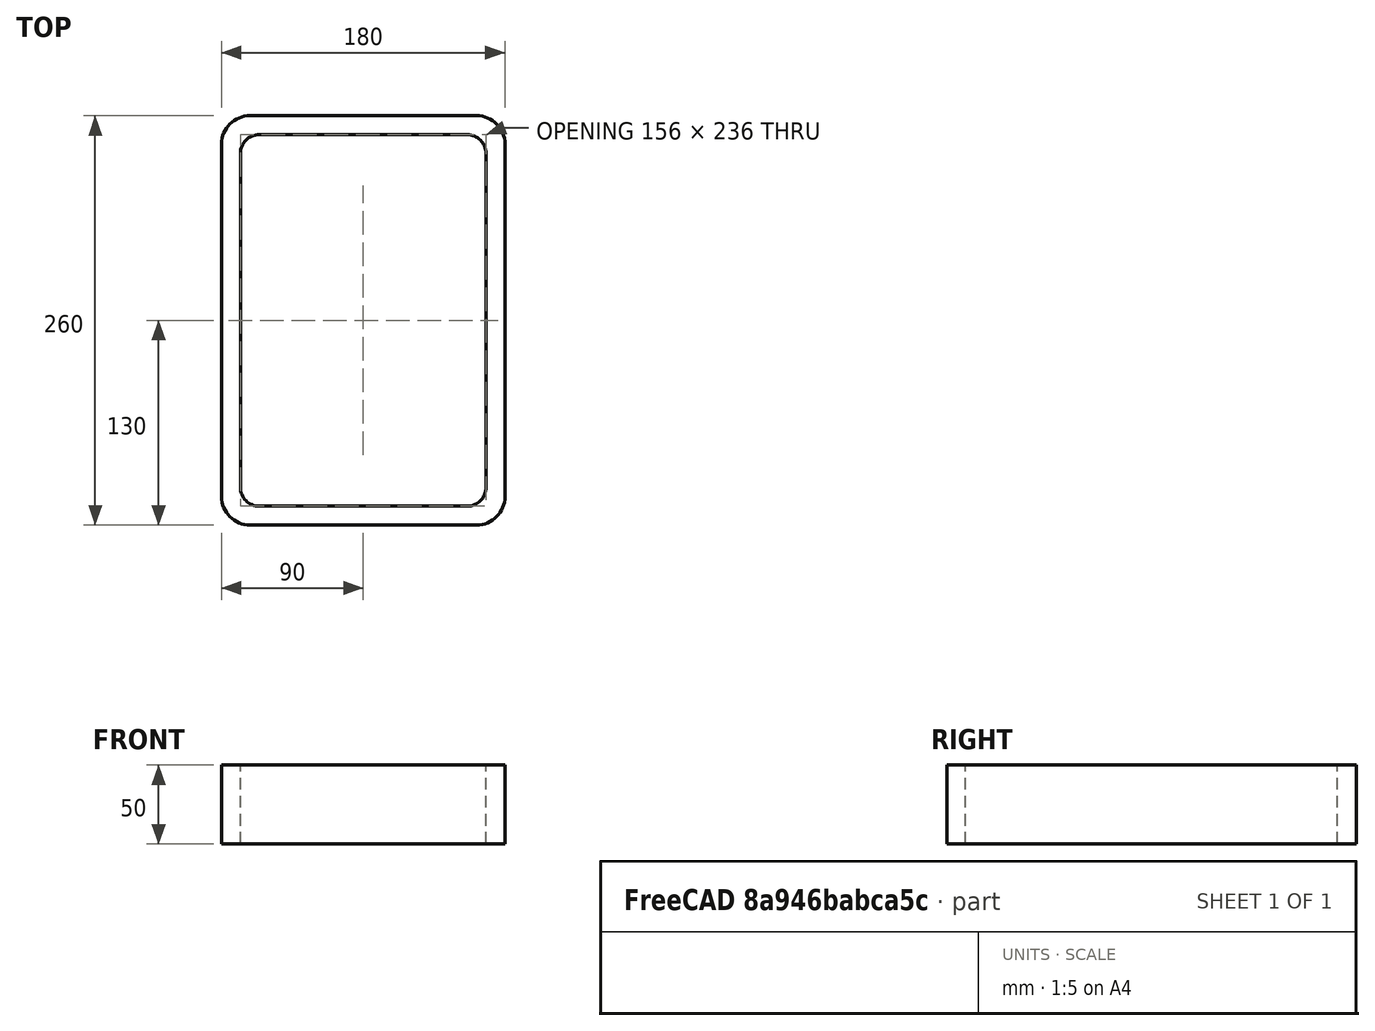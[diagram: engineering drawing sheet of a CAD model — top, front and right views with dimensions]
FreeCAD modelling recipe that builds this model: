
FCSTD DOCUMENT  (FreeCAD 0.15R4671 (Git))
Label: Rectangular hollow section 260x180x12 EN10219 S235JRH
License: All rights reserved
LicenseURL: http://en.wikipedia.org/wiki/All_rights_reserved
objects: Sketcher::SketchObject×1, Part::Extrusion×1
note: 2 computed .brp shape members not serialized (recipe doc carries the construction recipe); baked Part::Feature solids carry a one-line shape summary decoded from their .brp

FEATURE [Sketcher::SketchObject] Sketch
  sketch-geometry (16):
    g0: LineSegment StartX=-66 StartY=118 StartZ=0 EndX=66 EndY=118 EndZ=0
    g1: LineSegment StartX=78 StartY=106 StartZ=0 EndX=78 EndY=-106 EndZ=0
    g2: LineSegment StartX=66 StartY=-118 StartZ=0 EndX=-66 EndY=-118 EndZ=0
    g3: LineSegment StartX=-78 StartY=-106 StartZ=0 EndX=-78 EndY=106 EndZ=0
    g4: LineSegment StartX=-72 StartY=130 StartZ=0 EndX=72 EndY=130 EndZ=0
    g5: LineSegment StartX=90 StartY=112 StartZ=0 EndX=90 EndY=-112 EndZ=0
    g6: LineSegment StartX=72 StartY=-130 StartZ=0 EndX=-72 EndY=-130 EndZ=0
    g7: LineSegment StartX=-90 StartY=-112 StartZ=0 EndX=-90 EndY=112 EndZ=0
    g8: ArcOfCircle CenterX=-66 CenterY=106 CenterZ=0 NormalX=0 NormalY=0 NormalZ=1 Radius=12 StartAngle=1.5708 EndAngle=3.14159
    g9: ArcOfCircle CenterX=66 CenterY=106 CenterZ=0 NormalX=0 NormalY=0 NormalZ=1 Radius=12 StartAngle=0 EndAngle=1.5708
    g10: ArcOfCircle CenterX=66 CenterY=-106 CenterZ=0 NormalX=0 NormalY=0 NormalZ=1 Radius=12 StartAngle=4.71239 EndAngle=6.28319
    g11: ArcOfCircle CenterX=-66 CenterY=-106 CenterZ=0 NormalX=0 NormalY=0 NormalZ=1 Radius=12 StartAngle=3.14159 EndAngle=4.71239
    g12: ArcOfCircle CenterX=72 CenterY=112 CenterZ=0 NormalX=0 NormalY=0 NormalZ=1 Radius=18 StartAngle=0 EndAngle=1.5708
    g13: ArcOfCircle CenterX=72 CenterY=-112 CenterZ=0 NormalX=0 NormalY=0 NormalZ=1 Radius=18 StartAngle=4.71239 EndAngle=6.28319
    g14: ArcOfCircle CenterX=-72 CenterY=-112 CenterZ=0 NormalX=0 NormalY=0 NormalZ=1 Radius=18 StartAngle=3.14159 EndAngle=4.71239
    g15: ArcOfCircle CenterX=-72 CenterY=112 CenterZ=0 NormalX=0 NormalY=0 NormalZ=1 Radius=18 StartAngle=1.5708 EndAngle=3.14159
  constraints (36):
    c: Horizontal(g2)
    c: Vertical(g3)
    c: Horizontal(g6)
    c: Vertical(g7)
    c: Tangent(g3,g8) = 1.5708
    c: Tangent(g0,g8) = 1.5708
    c: Tangent(g0,g9) = 1.5708
    c: Tangent(g1,g9) = 1.5708
    c: Tangent(g1,g10) = 1.5708
    c: Tangent(g2,g10) = 1.5708
    c: Tangent(g2,g11) = 1.5708
    c: Tangent(g3,g11) = 1.5708
    c: Tangent(g4,g12) = 1.5708
    c: Tangent(g5,g12) = 1.5708
    c: Tangent(g5,g13) = 1.5708
    c: Tangent(g6,g13) = 1.5708
    c: Tangent(g6,g14) = 1.5708
    c: Tangent(g7,g14) = 1.5708
    c: Tangent(g7,g15) = 1.5708
    c: Tangent(g4,g15) = 1.5708
    c: Equal(g9,g8)
    c: Equal(g9,g11)
    c: Equal(g9,g10)
    c: Equal(g12,g15)
    c: Equal(g12,g14)
    c: Equal(g12,g13)
    c: Symmetric(g4,g6,g-1)
    c: Symmetric(g7,g5,g-2)
    c: DistanceY(g4,g6) = -260
    c: DistanceX(g7,g5) = 180
    c: Symmetric(g3,g1,g-2)
    c: Symmetric(g0,g2,g-1)
    c: DistanceY(g0,g4) = 12
    c: DistanceX(g5,g1) = -12
    c: Radius(g9) = 12
    c: Radius(g12) = 18
FEATURE [Part::Extrusion] Extrude  label="Rectangular hollow section 260x180x12 EN10219 S235JRH"
  Base = -> Sketch
  Dir = (0,0,50)
  Solid = true
